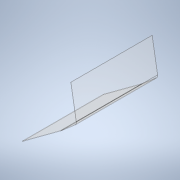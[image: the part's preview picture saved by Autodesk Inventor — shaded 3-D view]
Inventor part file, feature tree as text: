
AUTODESK INVENTOR PART (.ipt)
format: ipt  version: 2020.2 (Build 242310000, 310)  size: 112,640 bytes
history: native  units: mm
features: other x1, extrude x1, sketch x1
ambient origin geometry x8: Origin, YZ Plane, XZ Plane, XY Plane, X Axis, Y Axis, Z Axis, Center Point
bodies: Body1 (feature_tree)
feature tree (3):
  other  "ソリッド1"
  extrude  "押し出し1"  Depth=98.8mm TaperAngle=0.0deg
  sketch  "スケッチ1"
